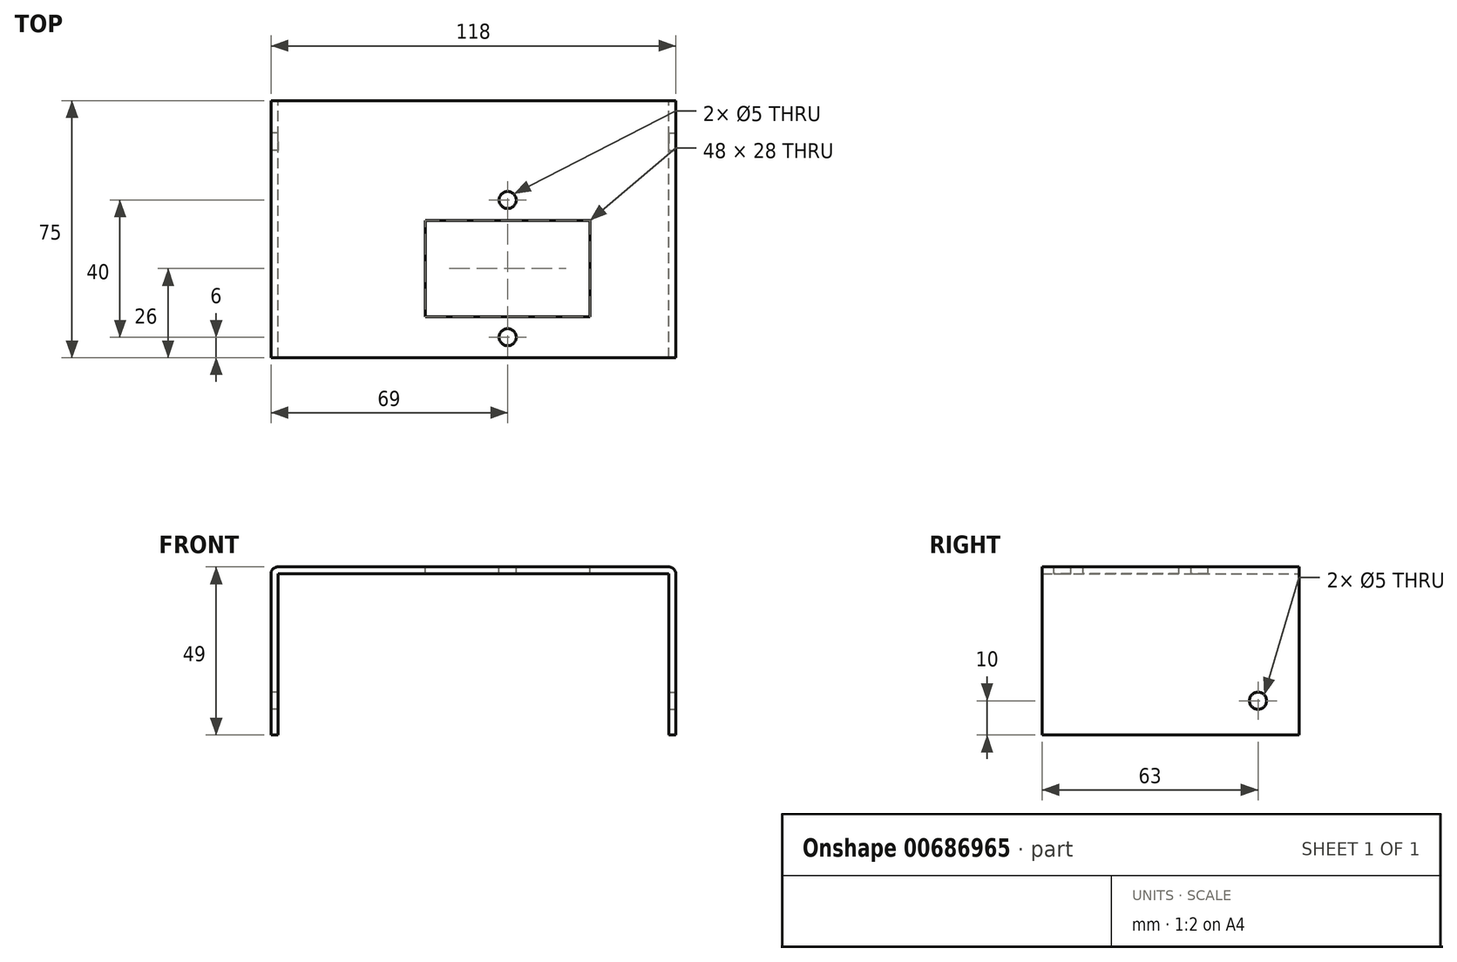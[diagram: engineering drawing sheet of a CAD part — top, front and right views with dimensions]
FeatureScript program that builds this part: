
annotation { "Feature Type Name" : "Feature", "Feature Type Description" : "" }
export const myFeature = defineFeature(function(context is Context, id is Id, definition is map)
    precondition{}
    {
        {
            var Q0;
            Q0=qCreatedBy(makeId("Top.planeOp"),FACE);
            var sketch = newSketch(context, id + "F0", { "sketchPlane" : qUnion([Q0])});
            skLineSegment(sketch, "E0.bottom", {"start": v(59, 37.5) * mm, "end": v(-59, 37.5) * mm});
            skLineSegment(sketch, "E0.top", {"start": v(59, -37.5) * mm, "end": v(-59, -37.5) * mm});
            skLineSegment(sketch, "E0.left", {"start": v(59, 37.5) * mm, "end": v(59, -37.5) * mm});
            skLineSegment(sketch, "E0.right", {"start": v(-59, 37.5) * mm, "end": v(-59, -37.5) * mm});
            skPoint(sketch, "E0.middle", {"position": v(0, 0) * mm});
            skSolve(sketch);
        }
        {
            var Q0;
            Q0=makeQuery(id+"F0.imprint","IMPRINT",FACE,{"disambiguationData":[TD([[makeQuery(id+"F0.imprint","IMPRINT",EDGE,{"derivedFrom":sQuery(id+"F0.wireOp",EDGE,"E0.bottom")}),1.0]])]});
            extrude(context, id + "F1", {"entities" : qUnion([Q0]), "depth" : 2 * mm, "offsetDistance" : 25 * mm});
        }
        {
            var Q0;
            Q0=makeQuery(id+"F1.opExtrude","CAP_FACE",FACE,{"disambiguationData":[OSD([sQuery(id+"F0.wireOp",EDGE,"E0.bottom"),sQuery(id+"F0.wireOp",EDGE,"E0.top"),sQuery(id+"F0.wireOp",EDGE,"E0.left"),sQuery(id+"F0.wireOp",EDGE,"E0.right")])],"isStart":false});
            var sketch = newSketch(context, id + "F2", { "sketchPlane" : qUnion([Q0])});
            skLineSegment(sketch, "E1.top", {"start": v(-14, -25.5) * mm, "end": v(34, -25.5) * mm});
            skLineSegment(sketch, "E1.left", {"start": v(-14, 2.5) * mm, "end": v(-14, -25.5) * mm});
            skLineSegment(sketch, "E1.right", {"start": v(34, 2.5) * mm, "end": v(34, -25.5) * mm});
            skCircle(sketch, "E2", {"center": v(10, -31.5) * mm, "radius": 2.5 * mm});
            skPoint(sketch, "E2.centerSnap0", {"position": v(10, -25.5) * mm});
            skLineSegment(sketch, "E3", {"start": v(-14, 2.5) * mm, "end": v(34, 2.5) * mm});
            skCircle(sketch, "E4", {"center": v(10, 8.5) * mm, "radius": 2.5 * mm});
            skPoint(sketch, "E4.centerSnap0", {"position": v(10, 2.5) * mm});
            skSolve(sketch);
        }
        {
            var Q0;
            Q0 = qSketchRegion(id + "F2", true);
            extrude(context, id + "F3", {"entities" : qUnion([Q0]), "operationType" : NewBodyOperationType.REMOVE, "oppositeDirection" : true, "depth" : 25 * mm, "offsetDistance" : 25 * mm});
        }
        {
            var Q0;
            Q0=makeQuery(id+"F1.opExtrude","CAP_FACE",FACE,{"disambiguationData":[OSD([sQuery(id+"F0.wireOp",EDGE,"E0.bottom"),sQuery(id+"F0.wireOp",EDGE,"E0.top"),sQuery(id+"F0.wireOp",EDGE,"E0.left"),sQuery(id+"F0.wireOp",EDGE,"E0.right")])],"isStart":true});
            var sketch = newSketch(context, id + "F4", { "sketchPlane" : qUnion([Q0])});
            skLineSegment(sketch, "E5.bottom", {"start": v(-59, 37.5) * mm, "end": v(-57, 37.5) * mm});
            skLineSegment(sketch, "E5.top", {"start": v(-59, -37.5) * mm, "end": v(-57, -37.5) * mm});
            skLineSegment(sketch, "E5.left", {"start": v(-59, 37.5) * mm, "end": v(-59, -37.5) * mm});
            skLineSegment(sketch, "E5.right", {"start": v(-57, 37.5) * mm, "end": v(-57, -37.5) * mm});
            skLineSegment(sketch, "E6.bottom", {"start": v(59, 37.5) * mm, "end": v(57, 37.5) * mm});
            skLineSegment(sketch, "E6.top", {"start": v(59, -37.5) * mm, "end": v(57, -37.5) * mm});
            skLineSegment(sketch, "E6.left", {"start": v(59, 37.5) * mm, "end": v(59, -37.5) * mm});
            skLineSegment(sketch, "E6.right", {"start": v(57, 37.5) * mm, "end": v(57, -37.5) * mm});
            skSolve(sketch);
        }
        {
            var Q0;
            Q0 = qSketchRegion(id + "F4", true);
            extrude(context, id + "F5", {"entities" : qUnion([Q0]), "operationType" : NewBodyOperationType.ADD, "depth" : 47 * mm, "offsetDistance" : 25 * mm});
        }
        {
            var Q0;
            Q0=makeQuery(id+"F1.opExtrude","CAP_EDGE",EDGE,{"disambiguationData":[OSD([sQuery(id+"F0.wireOp",EDGE,"E0.left")])],"isStart":false});
            var Q1;
            Q1=makeQuery(id+"F1.opExtrude","CAP_EDGE",EDGE,{"disambiguationData":[OSD([sQuery(id+"F0.wireOp",EDGE,"E0.right")])],"isStart":false});
            fillet(context, id + "F6", {"entities" : qUnion([Q0, Q1]), "radius" : 2 * mm, "tangentPropagation" : true, "allowEdgeOverflow" : false});
        }
        {
            var Q0;
            Q0=makeQuery(id+"F5.boolean.opBoolean","MERGE",FACE,{"derivedFrom":[makeQuery(id+"F1.opExtrude","SWEPT_FACE",FACE,{"disambiguationData":[OSD([sQuery(id+"F0.wireOp",EDGE,"E0.right")])]}),makeQuery(id+"F5.opExtrude","SWEPT_FACE",FACE,{"disambiguationData":[OSD([sQuery(id+"F4.wireOp",EDGE,"E5.left")])]})]});
            var sketch = newSketch(context, id + "F7", { "sketchPlane" : qUnion([Q0])});
            skCircle(sketch, "E7", {"center": v(-25.5, -37) * mm, "radius": 2.5 * mm});
            skSolve(sketch);
        }
        {
            var Q0;
            Q0=makeQuery(id+"F7.imprint","IMPRINT",FACE,{"disambiguationData":[TD([[makeQuery(id+"F7.imprint","IMPRINT",EDGE,{"derivedFrom":sQuery(id+"F7.wireOp",EDGE,"E7")}),1.0]])]});
            extrude(context, id + "F8", {"entities" : qUnion([Q0]), "operationType" : NewBodyOperationType.REMOVE, "oppositeDirection" : true, "depth" : 25 * mm, "offsetDistance" : 25 * mm});
        }
        {
            var Q0;
            Q0=makeQuery(id+"F5.boolean.opBoolean","MERGE",FACE,{"derivedFrom":[makeQuery(id+"F1.opExtrude","SWEPT_FACE",FACE,{"disambiguationData":[OSD([sQuery(id+"F0.wireOp",EDGE,"E0.left")])]}),makeQuery(id+"F5.opExtrude","SWEPT_FACE",FACE,{"disambiguationData":[OSD([sQuery(id+"F4.wireOp",EDGE,"E6.left")])]})]});
            var sketch = newSketch(context, id + "F9", { "sketchPlane" : qUnion([Q0])});
            skCircle(sketch, "E8", {"center": v(25.5, -37) * mm, "radius": 2.5 * mm});
            skSolve(sketch);
        }
        {
            var Q0;
            Q0 = qSketchRegion(id + "F9", true);
            extrude(context, id + "F10", {"entities" : qUnion([Q0]), "operationType" : NewBodyOperationType.REMOVE, "oppositeDirection" : true, "depth" : 25 * mm, "offsetDistance" : 25 * mm});
        }
    });
